# Revit family: Spout_BasinBath_Abey_LuciaBuilders_165_FaceBased
name_source: partatom
category: Plumbing Fixtures
units: mm (PartAtom-declared; Revit-internal decimal feet)

## family parameters
Cut with Voids When Loaded = Yes
Host = Face
Maintain Annotation Orientation = No
OmniClass Number = 23.31.11.19
OmniClass Title = Faucet Mixing Valves
Part Type = Normal
Room Calculation Point = No
Round Connector Dimension = Use Diameter
Shared = No

## types (3) — shared parameters
Assembly Code = C1030210
CW Connection = Yes
Default Elevation = 1,050 mm
HW Connection = Yes
IfcExportAs = IfcValve
IfcExportType = FAUCET
Manufacturer = Abey
ManufacturerOverallDepth = 177.5 mm
ManufacturerOverallHeight = 110 mm
ManufacturerOverallWidth = 80 mm
ManufacturerURLProductSpecific = https://www.abeyspecifier.com.au
ModifiedIssue = 20251103 $
URL = https://www.abey.com.au
Uniclass2015Code = Pr_40_20_87_55
Uniclass2015Title = Mixer taps
Uniclass2015Version = Products v1.38
Vent Connection = No
Waste Connection = No
zero-valued in all types: Cost

## per-type parameters (varying)
| type | Description | ManufacturerSpecCode | Material | Model | Type Comments |
| Chrome (4CS-165-LF) | Lucia Builders 165mm Basin/Bath Spout Chrome | 4CS-165-LF | Metal_Abey_Chrome | 4CS-165-LF | Spout - Basin Bath - 165 - Chrome |
| Brushed Nickel (4CS-165-BN-LF) | Lucia Builders 165mm Basin/Bath Spout Brushed Nickel | 4CS-165-BN-LF | Metal_Abey_BrushedNickel | 4CS-165-BN-LF | Spout - Basin Bath - 165 - Brushed Nickel |
| Black (4CS-165-B-LF) | Lucia Builders 165mm Basin/Bath Spout Black | 4CS-165-B-LF | Metal_Abey_Black | 4CS-165-B-LF | Spout - Basin Bath - 165 - Black |

## geometry (parser evidence)
native form markers: Sweep x6
no freeform markers — native parametric forms only
